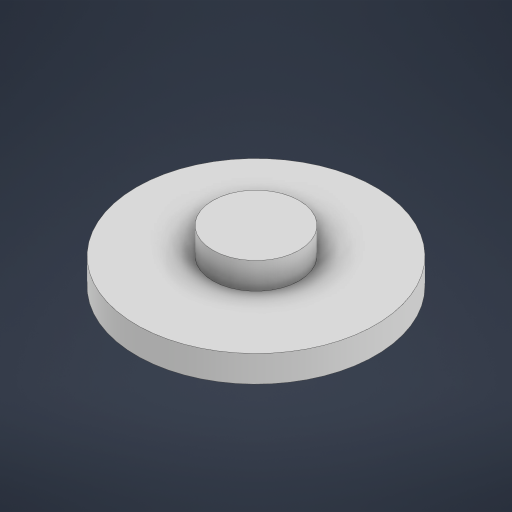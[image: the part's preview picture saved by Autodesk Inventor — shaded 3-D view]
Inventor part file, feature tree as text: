
AUTODESK INVENTOR PART (.ipt)
format: ipt  version: 2024 (Build 280153000, 153)  size: 179,200 bytes
history: native  units: mm
features: extrude x2, sketch x2
ambient origin geometry x8: Origin, YZ Plane, XZ Plane, XY Plane, X Axis, Y Axis, Z Axis, Center Point
bodies: Solid1 (feature_tree)
feature tree (4):
  extrude  "Extrusion1"  Depth=20.0mm TaperAngle=0.0deg
  extrude  "Extrusion2"  Depth=20.0mm TaperAngle=0.0deg
  sketch  "Sketch1"  dims[d0=180.0mm d1=20.0mm d2=0.0mm]
  sketch  "Sketch2"  dims[d3=65.0mm d4=20.0mm d5=0.0mm]
